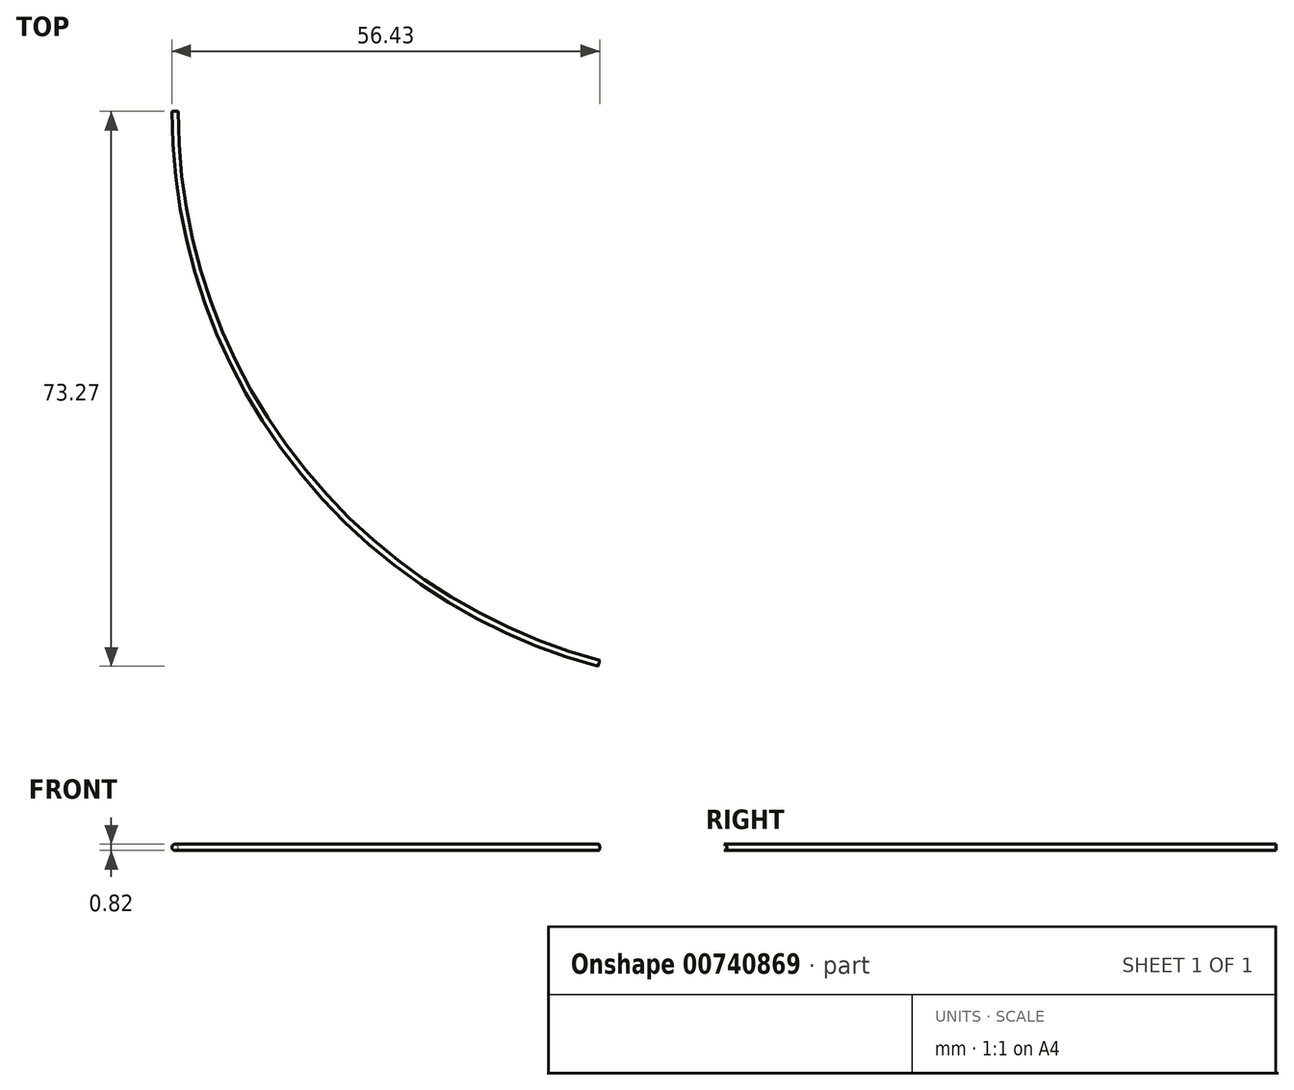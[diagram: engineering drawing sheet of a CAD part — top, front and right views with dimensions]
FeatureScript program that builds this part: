
annotation { "Feature Type Name" : "Feature", "Feature Type Description" : "" }
export const myFeature = defineFeature(function(context is Context, id is Id, definition is map)
    precondition{}
    {
        {
            var Q0;
            Q0=qCreatedBy(makeId("Front.planeOp"),FACE);
            var sketch = newSketch(context, id + "F0", { "sketchPlane" : qUnion([Q0])});
            skCircle(sketch, "E0", {"center": v(-75.45, 0) * mm, "radius": 0.4 * mm});
            skLineSegment(sketch, "E1", {"start": v(0, 0) * mm, "end": v(0, 1.19) * mm});
            skSolve(sketch);
        }
        {
            var Q0;
            Q0=makeQuery(id+"F0.imprint","IMPRINT",FACE,{"disambiguationData":[TD([[makeQuery(id+"F0.imprint","IMPRINT",EDGE,{"derivedFrom":sQuery(id+"F0.wireOp",EDGE,"E0")}),1.0]])]});
            var Q1;
            Q1=sQuery(id+"F0.wireOp",EDGE,"E1");
            revolve(context, id + "F1", {"surfaceOperationType" : NewSurfaceOperationType.NEW, "entities" : qUnion([Q0]), "axis" : qUnion([Q1]), "revolveType" : RevolveType.ONE_DIRECTION, "angle" : 75 * degree});
        }
    });
